annotation { "Feature Type Name" : "Feature", "Feature Type Description" : "" }
export const myFeature = defineFeature(function(context is Context, id is Id, definition is map)
    precondition{}
    {
        {
            var Q0;
            Q0=qCreatedBy(makeId("Top.planeOp"),FACE);
            var sketch = newSketch(context, id + "F0", { "sketchPlane" : qUnion([Q0])});
            skLineSegment(sketch, "E0.bottom", {"start": v(95.25, 95.25) * mm, "end": v(-95.25, 95.25) * mm});
            skLineSegment(sketch, "E0.top", {"start": v(95.25, -95.25) * mm, "end": v(-95.25, -95.25) * mm});
            skLineSegment(sketch, "E0.left", {"start": v(95.25, 95.25) * mm, "end": v(95.25, -95.25) * mm});
            skLineSegment(sketch, "E0.right", {"start": v(-95.25, 95.25) * mm, "end": v(-95.25, -95.25) * mm});
            skPoint(sketch, "E0.middle", {"position": v(0, 0) * mm});
            skSolve(sketch);
        }
        {
            var Q0;
            Q0=qCreatedBy(makeId("Top.planeOp"),FACE);
            var sketch = newSketch(context, id + "F1", { "sketchPlane" : qUnion([Q0])});
            skLineSegment(sketch, "E1", {"start": v(-88.9, 24.6) * mm, "end": v(88.9, 24.6) * mm});
            skLineSegment(sketch, "E2", {"start": v(88.9, 24.6) * mm, "end": v(88.9, -24.6) * mm});
            skLineSegment(sketch, "E3", {"start": v(88.9, -24.6) * mm, "end": v(-88.9, -24.6) * mm});
            skLineSegment(sketch, "E4", {"start": v(-88.9, -24.6) * mm, "end": v(-88.9, 24.6) * mm});
            skLineSegment(sketch, "E5", {"start": v(-88.9, 24.6) * mm, "end": v(88.9, -24.6) * mm, "construction": true});
            skPoint(sketch, "E6", {"position": v(0, 0) * mm});
            skSolve(sketch);
        }
        {
            var Q0;
            Q0 = qSketchRegion(id + "F1", true);
            extrude(context, id + "F2", {"entities" : qUnion([Q0]), "depth" : 1.59 * mm, "offsetDistance" : 25.4 * mm});
        }
        {
            var Q0;
            Q0=makeQuery(id+"F2.opExtrude","SWEPT_FACE",FACE,{"disambiguationData":[OSD([sQuery(id+"F1.wireOp",EDGE,"E2")])]});
            var sketch = newSketch(context, id + "F3", { "sketchPlane" : qUnion([Q0])});
            skLineSegment(sketch, "E7", {"start": v(-24.6, 0) * mm, "end": v(-24.13, 1.59) * mm});
            skLineSegment(sketch, "E8", {"start": v(-24.13, 1.59) * mm, "end": v(-24.6, 1.59) * mm});
            skLineSegment(sketch, "E9", {"start": v(-24.6, 1.59) * mm, "end": v(-24.6, 0) * mm});
            skLineSegment(sketch, "E10", {"start": v(24.6, 1.59) * mm, "end": v(24.13, 1.59) * mm});
            skLineSegment(sketch, "E11", {"start": v(24.13, 1.59) * mm, "end": v(24.6, 0) * mm});
            skLineSegment(sketch, "E12", {"start": v(24.6, 0) * mm, "end": v(24.6, 1.59) * mm});
            skSolve(sketch);
        }
        {
            var Q0;
            Q0 = qSketchRegion(id + "F3", true);
            extrude(context, id + "F4", {"entities" : qUnion([Q0]), "operationType" : NewBodyOperationType.REMOVE, "endBound" : BoundingType.THROUGH_ALL, "oppositeDirection" : true, "depth" : 25.4 * mm, "offsetDistance" : 25.4 * mm});
        }
        {
            var Q0;
            Q0=makeQuery(id+"F2.opExtrude","CAP_FACE",FACE,{"disambiguationData":[OSD([sQuery(id+"F1.wireOp",EDGE,"E1"),sQuery(id+"F1.wireOp",EDGE,"E2"),sQuery(id+"F1.wireOp",EDGE,"E3"),sQuery(id+"F1.wireOp",EDGE,"E4")])],"isStart":false});
            var sketch = newSketch(context, id + "F5", { "sketchPlane" : qUnion([Q0])});
            skText(sketch, "E13", { "text": "Larry Snyder", "fontName": "RobotoSlab-Bold.ttf"});
            skText(sketch, "E14", { "text": "Attorney at Law", "fontName": "RobotoSlab-Bold.ttf"});
            const initialGuessF5  = {"E13": [-0.08573, 0.00014, 1, 0, 0.01978], "E14": [-0.0381, -0.01441, 1, 0, 0.00722]};
            skSetInitialGuess(sketch, initialGuessF5);
            skSolve(sketch);
        }
        {
            var Q0;
            Q0 = qSketchRegion(id + "F5", true);
            extrude(context, id + "F6", {"entities" : qUnion([Q0]), "operationType" : NewBodyOperationType.REMOVE, "oppositeDirection" : true, "depth" : 0.8 * mm, "offsetDistance" : 25.4 * mm});
        }
    });